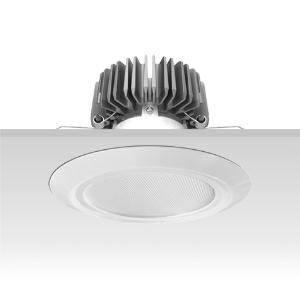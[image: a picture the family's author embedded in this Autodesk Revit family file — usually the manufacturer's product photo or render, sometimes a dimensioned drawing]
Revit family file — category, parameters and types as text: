
# Revit family: 3f_filippi_-_3f_reno_bianco_ampio_3f_filippi_-_30650_a01048_-_3f_reno_200_wh_2000-930_ep_wide___smp_wh_9b90
name_source: partatom
category: Lighting Fixtures
units: mm (PartAtom-declared; Revit-internal decimal feet)

## family parameters
Cut with Voids When Loaded = No
Host = Face
Light Source = No
Part Type = Normal
Room Calculation Point = No
Round Connector Dimension = Use Diameter
Shared = No

## types (1)
- 3F Filippi - 3F Reno Bianco Ampio (1 x LED, 1650 lm, 25 W, 3000 K)
    Apparent Load = 25 VA
    Approval mark = ENEC
    CIE Flux Codes = 74 92 98 100 100
    Color Rendering = 90
    Color Temperature = 3000 K
    Control Gear = Electronic ballast
    Default Elevation = 1800 mm
    Description = ILLUMINOTECHNICAL
Luminous efficiency 100% (DLOR 100%, ULOR 0%).
Initial luminous flux of the luminaire 1650 lm.
Emergency luminaire luminous flux BLF 16.7%.
Direct symmetric wide distribution.
Installation Interdistance Transv.D = 1.06 x hu - Long.D = 1.04 x hu.
Average luminance <3000 cd/m² for radial angles >65°.
Tabular UGR (CIE 117 - 4H-8H; S=0.25H; 70/50/20): RUG 21.3 - 21.1.
Beam angle: 70° - 69°.
Luminous efficacy 66 lm/W.
Lifetime (L90/B10): 30000 h. (tq+25°C)
Lifetime (L85/B10): 50000 h. (tq+25°C)
Lifetime (L70/B10): 80000 h. (tq+25°C)
Sudden decreased luminous flux after 50000 hours: 0% (C0).
Photobiological safety in compliance with IEC/TR 62778: RG0 risk exempt, (IEC 62471).
In compliance with IEC/EN 62722-2-1 - IEC/EN 62717 standards.

SOURCE
Compact LED module 2000/930.
Energy efficiency class (UE 2019/2020 - UE 2019/2015): E.
CIE 13.3 Colour rendering index: CRI >90 (R9 >50%).
IES TM-30 Fidelity Index: Rf = 92 Rg = 101.
CCT nominal colour temperature 3000 K.
Colour initial tolerance (MacAdam): SDCM 3.
Zhaga Book 3 compliant.

MECHANICAL
Passive heat dissipator in die-casting aluminium, oversized, for optimum thermal management of the LED module.
Parabolic element with graduated/concentric rings in white polycarbonate.
Transparent external lens with glossy and satin differentiated surfaces, with a cooling and anti-insect system in methacrylate (PMMA).
Fastening spring clips in stainless steel.
Dimensions: diameter 226 mm, height 146 mm. Weight 1.555 kg.
IP44 protection degree for exposed part, IP20 for recessed part.
Mechanical strength to impacts IK05 (0.7 joule).
Glow-wire test resistance 650°C.

ELECTRICAL
Wiring on a separate unit.
Halogen Free electronic wiring 230V-50/60Hz, power factor 0.90, THD <25%, constant output current, SELV, class II, 1 driver.
Power of the luminaire 25 W.
CE - IEC 60598-1 - EN 60598-1.
EP maintained emergency wiring on board, 1h duration, 24h recharge; compliant with EN 60598-2-22, excluding high risk areas.
SAFE FLICKER: PstLM=<1 and SVM=<0.4 (IEC TR 61547-1 and IEC TR 63158), to ensure a more comfortable and safe light.
Ambient temperature from +5°C to +25°C.
Temperature class T6 max 85°C.
Relative humidity UR: <85%.

INSTALLATION
Pull-up recessed fitting.
False ceiling carving: 200 mm.
All accessories dedicated to this product are available on the Catalog and on our website www.3F-Filippi.com.

ACCESSORIES
A01048 - Anti-glare microprismatic SMP diffuser in methacrylate (PMMA), locked and in line with the trim, in white polycarbonate.

APPLICATIONS
Suitable product for food production plants (HACCP), IFS (Food Version 6), BRC (GSFS Food Version 7).
Environments: architectural, commercial, exhibition areas, transit areas, corridors, shops, display windows, service areas.
In false ceilings with narrow voids.

WARNING
Luminaire designed for disposal/recycling at end-of-life.
Replaceable (LED only) light source by a professional. Replaceable control gear by a professional.
    Height = 0 mm  [stored 0 ft]
    Lamp = 1 x LED
    Lamp Light Flux = 1650 lm
    Lamp Power = 25 W
    Lamp count = 1
    Length = 226 mm
    Lifetime = 50000 h
    Luminous efficacy = 66 lm/W
    Manufacturer = 3F Filippi
    ModVariant = No
    Model = 3F Filippi - 30650+A01048 - 3F Reno 200 WH 2000-930 EP WIDE + SMP WH
    Mounting Place = Ceiling
    Mounting Type = Recessed
    Number of Poles = 1
    OnlyDefault = Yes
    Power Factor = 1
    Product Name = 3F Filippi - 3F Reno Bianco Ampio
    Product group = recessed luminaire
    ProductGroupID = 4
    Protection Class = Protection class II
    Protection Degree = IP 20
    RLX_Detail_Level = 1
    RLX_Emergency_Light_Flux = 0 lm
    RLX_Emergency_Type = 0
    RLX_Emergency_Type_DB = No
    RlxData = <blob elided: 94641 chars, md5=7c5dd84c>
    Socket = socket
    Standby Power = 0 W
    System Light Flux = 1650 lm
    System Power = 25 W
    Type Comments = Product without accessories
    Type Image = 3ffilippi_3f_reno_200_wh_vs_smp.jpg
    URL = http://relux.com
    VarID = ---
    Voltage = 0 V
    Weight = 0.00 kg
    Width = 0 mm  [stored 0 ft]

note: [stored X ft] marks values corroborated as IEEE doubles in the binary element streams (Revit-internal decimal feet)

## geometry (parser evidence)
native form markers: Blend x4, Sweep x10
no freeform markers — native parametric forms only
